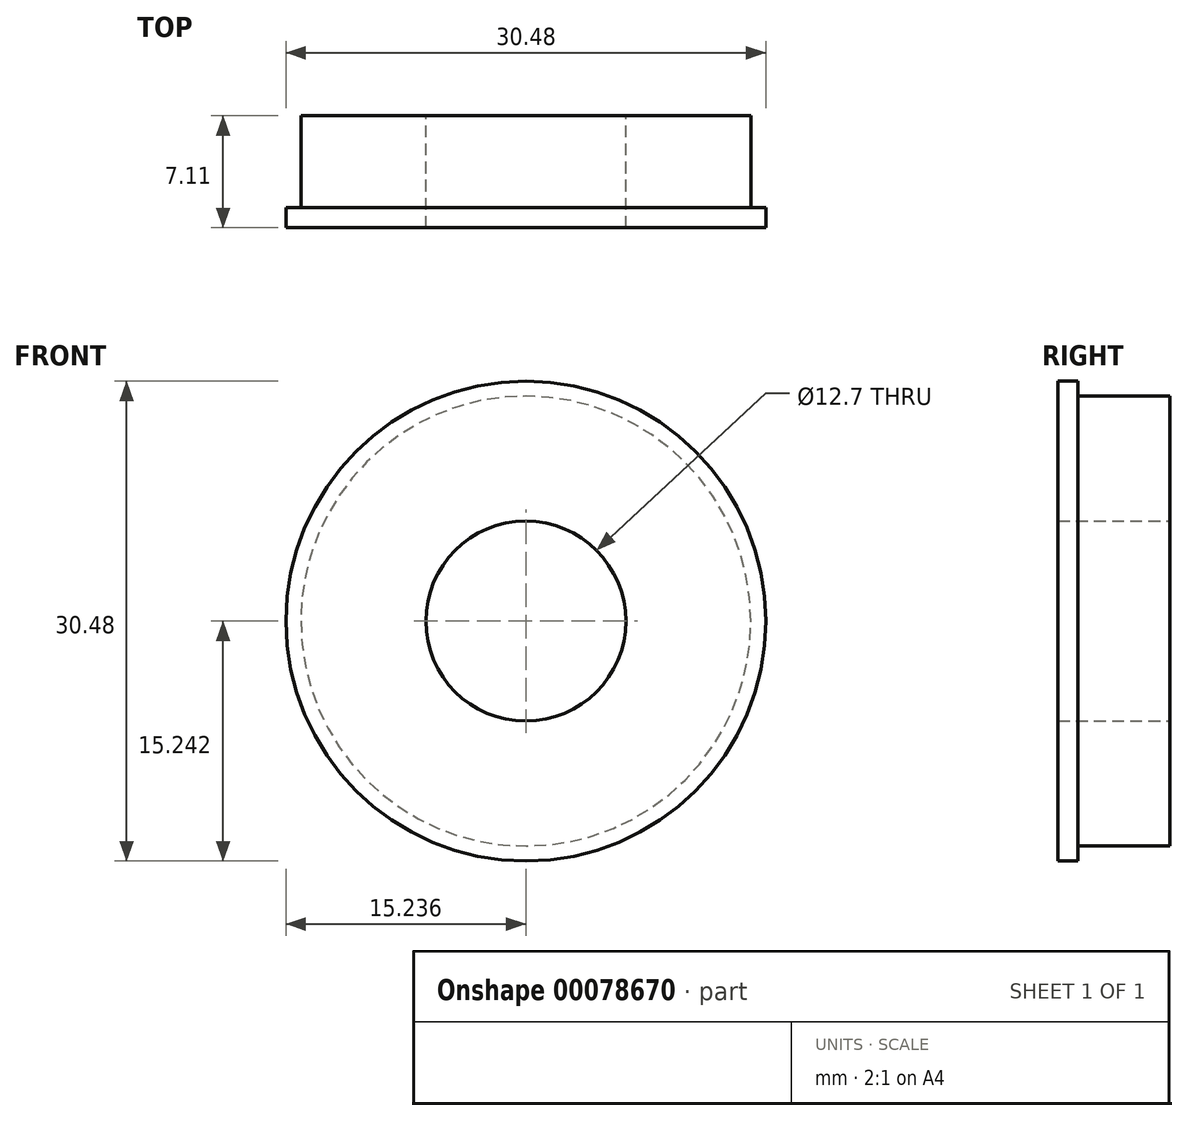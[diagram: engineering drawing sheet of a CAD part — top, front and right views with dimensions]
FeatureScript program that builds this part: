
annotation { "Feature Type Name" : "Feature", "Feature Type Description" : "" }
export const myFeature = defineFeature(function(context is Context, id is Id, definition is map)
    precondition{}
    {
        {
            var Q0;
            Q0=qCreatedBy(makeId("Front.planeOp"),FACE);
            var sketch = newSketch(context, id + "F0", { "sketchPlane" : qUnion([Q0])});
            skCircle(sketch, "E0", {"center": v(-66.25, 44.38) * mm, "radius": 14.29 * mm});
            skCircle(sketch, "E1", {"center": v(-66.25, 44.38) * mm, "radius": 6.35 * mm});
            skSolve(sketch);
        }
        {
            var Q0;
            Q0 = qSketchRegion(id + "F0", true);
            extrude(context, id + "F1", {"entities" : qUnion([Q0]), "depth" : 7.11 * mm});
        }
        {
            var Q0;
            Q0=makeQuery(id+"F1.opExtrude","CAP_FACE",FACE,{"disambiguationData":[OSD([sQuery(id+"F0.wireOp",EDGE,"E0"),sQuery(id+"F0.wireOp",EDGE,"E1")])],"isStart":false});
            var sketch = newSketch(context, id + "F2", { "sketchPlane" : qUnion([Q0])});
            skCircle(sketch, "E2", {"center": v(-66.25, 44.38) * mm, "radius": 15.24 * mm});
            skSolve(sketch);
        }
        {
            var Q0;
            Q0 = qSketchRegion(id + "F2", true);
            extrude(context, id + "F3", {"entities" : qUnion([Q0]), "operationType" : NewBodyOperationType.ADD, "oppositeDirection" : true, "depth" : 1.27 * mm});
        }
        {
            var Q0;
            Q0=makeQuery(id+"F3.boolean.opBoolean","MERGE",FACE,{"derivedFrom":[makeQuery(id+"F1.opExtrude","CAP_FACE",FACE,{"disambiguationData":[OSD([sQuery(id+"F0.wireOp",EDGE,"E0"),sQuery(id+"F0.wireOp",EDGE,"E1")])],"isStart":false}),makeQuery(id+"F3.opExtrude","CAP_FACE",FACE,{"disambiguationData":[OSD([sQuery(id+"F2.wireOp",EDGE,"E2")])],"isStart":true})]});
            var sketch = newSketch(context, id + "F4", { "sketchPlane" : qUnion([Q0])});
            skCircle(sketch, "E3", {"center": v(-66.25, 44.38) * mm, "radius": 6.35 * mm});
            skSolve(sketch);
        }
        {
            var Q0;
            Q0 = qSketchRegion(id + "F4", true);
            extrude(context, id + "F5", {"entities" : qUnion([Q0]), "operationType" : NewBodyOperationType.REMOVE, "oppositeDirection" : true, "depth" : 25.4 * mm});
        }
    });
